# Revit family: Artek_Bar Stools_Atelier Bar Stool _Atelier Bar Stool_quick_ship
name_source: partatom
category: Furniture
revit_build: Autodesk Revit 2018 (Build: 20170223_1515(x64)
units: mm (PartAtom-declared; Revit-internal decimal feet)

## family parameters
Always vertical = Yes
Cut with Voids When Loaded = No
OmniClass Number = 23.40.20.14.14.17
OmniClass Title = Stools
Room Calculation Point = No
Shared = No
Work Plane-Based = No

## types (12) — shared parameters
AssetType = Movable
BIMObjectName = Artek_Bar Stools_Atelier Bar Stool _Atelier Bar Stool
Brand = Artek
Category = Bar Stools
Collection = Atelier Bar Stool
Designer = TAF Studio
DurationUnit = Years
IfcExportAs = IfcFurnishingElementType
IfcExportType = CHAIR
Manufacturer = Artek
ManufacturerName = Artek
ManufacturerURL = https://www.artek.fi
Material = Wood
NBSDescription = Domestic chairs
NBSReference = 45-35-20/365
Name = Atelier Bar Stool
NominalDepth = 320 mm
NominalLength = 397 mm
Shape = Sculptured
URL = https://www.artek.fi
Uniclass2 = Pr_40_50_12_83
Uniclass2015Description = Stools
Uniclass2015Reference = Pr_40_50_12_85
Version = 1
VersionDate = 11/3/2020
WarrantyDurationUnit = Years
zero-valued in all types: Cost

## per-type parameters (varying)
| type | ChairMainMaterial | Color | ConvergoRefNr | HighestSeatingHeight | LowestSeatingHeight | MainColor | ModelNumber | NominalHeight | SeatingHeight | Size | StoolControl |
| Atelier Bar Stool 28104601 | Natural Beech | Natural beech | 0190-2009-0051-FI | 650 mm  [stored 2.13255 ft] | 650 mm  [stored 2.13255 ft] | Natural beech | 28104601 | 650 mm  [stored 2.13255 ft] | 650 mm  [stored 2.13255 ft] | 400x650x320 mm | atelier_bar_stool_65 |
| Atelier Bar Stool 28104602 | Natural Ash | Natural ash | 0190-2009-0051-FI | 650 mm  [stored 2.13255 ft] | 650 mm  [stored 2.13255 ft] | Natural ash | 28104602 | 650 mm  [stored 2.13255 ft] | 650 mm  [stored 2.13255 ft] | 400x650x320 mm | atelier_bar_stool_65 |
| Atelier Bar Stool 28104603 | Natural oak | Natural oak | 0190-2009-0051-FI | 650 mm  [stored 2.13255 ft] | 650 mm  [stored 2.13255 ft] | Natural oak | 28104603 | 650 mm  [stored 2.13255 ft] | 650 mm  [stored 2.13255 ft] | 400x650x320 mm | atelier_bar_stool_65 |
| Atelier Bar Stool 28104604 | Black beech | Black | 0190-2009-0051-FI | 650 mm  [stored 2.13255 ft] | 650 mm  [stored 2.13255 ft] | Black | 28104604 | 650 mm  [stored 2.13255 ft] | 650 mm  [stored 2.13255 ft] | 400x650x320 mm | atelier_bar_stool_65 |
| Atelier Bar Stool 28104605 | Dark red Beech | Dark red | 0190-2009-0051-FI | 650 mm  [stored 2.13255 ft] | 650 mm  [stored 2.13255 ft] | Dark red | 28104605 | 650 mm  [stored 2.13255 ft] | 650 mm  [stored 2.13255 ft] | 400x650x320 mm | atelier_bar_stool_65 |
| Atelier Bar Stool 28104606 | Green Beech | Green | 0190-2009-0051-FI | 650 mm  [stored 2.13255 ft] | 650 mm  [stored 2.13255 ft] | Green | 28104606 | 650 mm  [stored 2.13255 ft] | 650 mm  [stored 2.13255 ft] | 400x650x320 mm | atelier_bar_stool_65 |
| Atelier Bar Stool 28104701 | Natural Beech | Natural beech | 0190-2009-0052-FI | 750 mm  [stored 2.46063 ft] | 750 mm  [stored 2.46063 ft] | Natural beech | 28104701 | 750 mm  [stored 2.46063 ft] | 750 mm  [stored 2.46063 ft] | 400x750x320 mm | atelier_bar_stool_75 |
| Atelier Bar Stool 28104702 | Natural Ash | Natural ash | 0190-2009-0052-FI | 750 mm  [stored 2.46063 ft] | 750 mm  [stored 2.46063 ft] | Natural ash | 28104702 | 750 mm  [stored 2.46063 ft] | 750 mm  [stored 2.46063 ft] | 400x750x320 mm | atelier_bar_stool_75 |
| Atelier Bar Stool 28104703 | Natural oak | Natural oak | 0190-2009-0052-FI | 750 mm  [stored 2.46063 ft] | 750 mm  [stored 2.46063 ft] | Natural oak | 28104703 | 750 mm  [stored 2.46063 ft] | 750 mm  [stored 2.46063 ft] | 400x750x320 mm | atelier_bar_stool_75 |
| Atelier Bar Stool 28104704 | Black beech | Black | 0190-2009-0052-FI | 750 mm  [stored 2.46063 ft] | 750 mm  [stored 2.46063 ft] | Black | 28104704 | 750 mm  [stored 2.46063 ft] | 750 mm  [stored 2.46063 ft] | 400x750x320 mm | atelier_bar_stool_75 |
| Atelier Bar Stool 28104705 | Dark red Beech | Dark red | 0190-2009-0052-FI | 750 mm  [stored 2.46063 ft] | 750 mm  [stored 2.46063 ft] | Dark red | 28104705 | 750 mm  [stored 2.46063 ft] | 750 mm  [stored 2.46063 ft] | 400x750x320 mm | atelier_bar_stool_75 |
| Atelier Bar Stool 28104706 | Green Beech | Green | 0190-2009-0052-FI | 750 mm  [stored 2.46063 ft] | 750 mm  [stored 2.46063 ft] | Green | 28104706 | 750 mm  [stored 2.46063 ft] | 750 mm  [stored 2.46063 ft] | 400x750x320 mm | atelier_bar_stool_75 |

note: column(s) folded — value = type name in every type: Model

note: [stored X ft] marks values corroborated as IEEE doubles in the binary element streams (Revit-internal decimal feet)

## geometry (parser evidence)
native form markers: Sweep x8
no freeform markers — native parametric forms only
